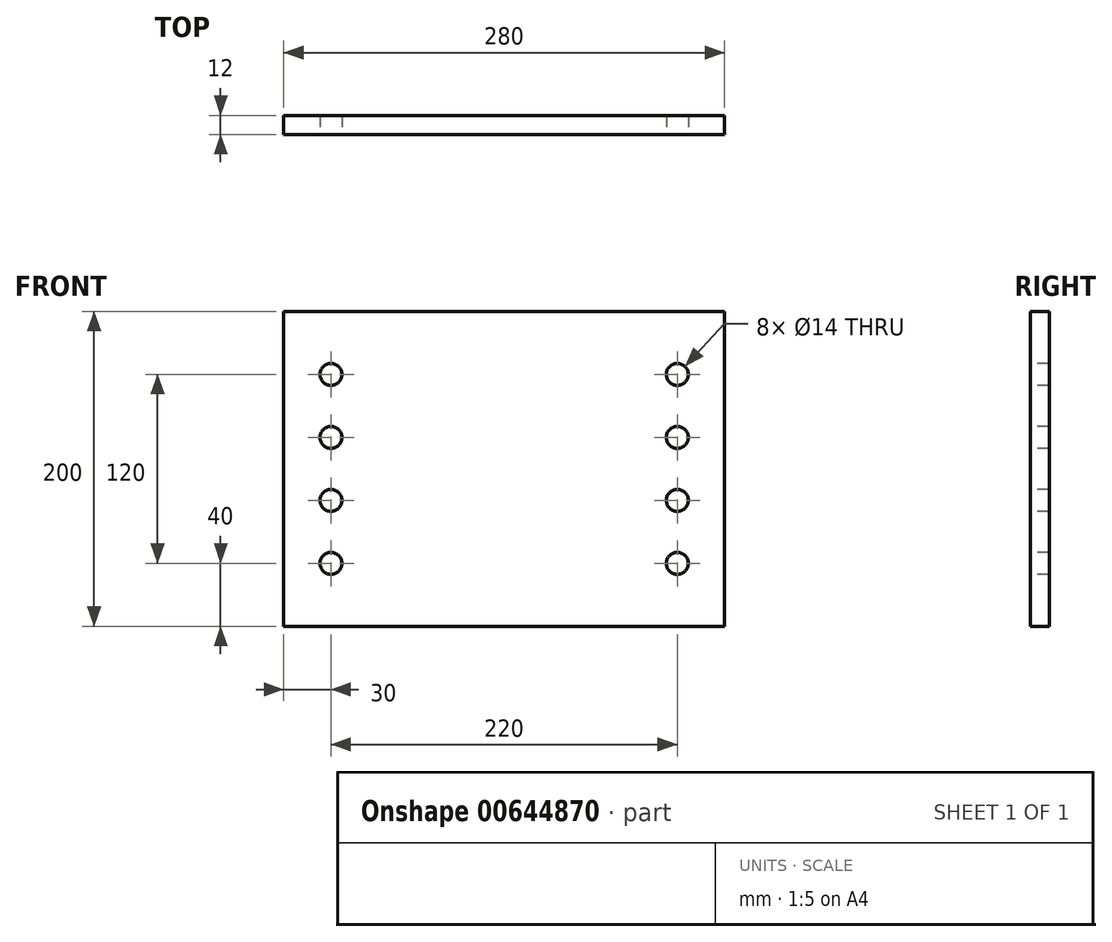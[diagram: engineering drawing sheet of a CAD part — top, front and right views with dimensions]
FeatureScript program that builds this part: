
annotation { "Feature Type Name" : "Feature", "Feature Type Description" : "" }
export const myFeature = defineFeature(function(context is Context, id is Id, definition is map)
    precondition{}
    {
        {
            var Q0;
            Q0=qCreatedBy(makeId("Front.planeOp"),FACE);
            var sketch = newSketch(context, id + "F0", { "sketchPlane" : qUnion([Q0])});
            skLineSegment(sketch, "E0.bottom", {"start": v(0, 0) * mm, "end": v(280, 0) * mm});
            skLineSegment(sketch, "E0.top", {"start": v(0, 200) * mm, "end": v(280, 200) * mm});
            skLineSegment(sketch, "E0.left", {"start": v(0, 0) * mm, "end": v(0, 200) * mm});
            skLineSegment(sketch, "E0.right", {"start": v(280, 0) * mm, "end": v(280, 200) * mm});
            skSolve(sketch);
        }
        {
            var Q0;
            Q0=makeQuery(id+"F0.imprint","IMPRINT",FACE,{"disambiguationData":[TD([[makeQuery(id+"F0.imprint","IMPRINT",EDGE,{"derivedFrom":sQuery(id+"F0.wireOp",EDGE,"E0.bottom")}),1.0]])]});
            extrude(context, id + "F1", {"entities" : qUnion([Q0]), "depth" : 12 * mm});
        }
        {
            var Q0;
            Q0=makeQuery(id+"F1.opExtrude","CAP_FACE",FACE,{"disambiguationData":[OSD([sQuery(id+"F0.wireOp",EDGE,"E0.bottom"),sQuery(id+"F0.wireOp",EDGE,"E0.top"),sQuery(id+"F0.wireOp",EDGE,"E0.left"),sQuery(id+"F0.wireOp",EDGE,"E0.right")])],"isStart":false});
            var sketch = newSketch(context, id + "F2", { "sketchPlane" : qUnion([Q0])});
            skLineSegment(sketch, "E1", {"start": v(30, 200) * mm, "end": v(30, 0) * mm});
            skLineSegment(sketch, "E2", {"start": v(250, 200) * mm, "end": v(250, 0) * mm});
            skLineSegment(sketch, "E3", {"start": v(0, 160) * mm, "end": v(280, 160) * mm});
            skLineSegment(sketch, "E4", {"start": v(0, 120) * mm, "end": v(280, 120) * mm});
            skLineSegment(sketch, "E5", {"start": v(0, 80) * mm, "end": v(280, 80) * mm});
            skLineSegment(sketch, "E6", {"start": v(0, 40) * mm, "end": v(280, 40) * mm});
            skPoint(sketch, "E7", {"position": v(30, 160) * mm});
            skPoint(sketch, "E8", {"position": v(30, 120) * mm});
            skPoint(sketch, "E9", {"position": v(30, 80) * mm});
            skPoint(sketch, "E10", {"position": v(30, 40) * mm});
            skPoint(sketch, "E11", {"position": v(250, 40) * mm});
            skPoint(sketch, "E12", {"position": v(250, 80) * mm});
            skPoint(sketch, "E13", {"position": v(250, 120) * mm});
            skPoint(sketch, "E14", {"position": v(250, 160) * mm});
            skSolve(sketch);
        }
        {
            var Q0;
            Q0=sQuery(id+"F2.wireOp",VERTEX,"E7");
            var Q1;
            Q1=sQuery(id+"F2.wireOp",VERTEX,"E8");
            var Q2;
            Q2=sQuery(id+"F2.wireOp",VERTEX,"E9");
            var Q3;
            Q3=sQuery(id+"F2.wireOp",VERTEX,"E10");
            var Q4;
            Q4=sQuery(id+"F2.wireOp",VERTEX,"E11");
            var Q5;
            Q5=sQuery(id+"F2.wireOp",VERTEX,"E12");
            var Q6;
            Q6=sQuery(id+"F2.wireOp",VERTEX,"E13");
            var Q7;
            Q7=sQuery(id+"F2.wireOp",VERTEX,"E14");
            var Q8;
            Q8=makeQuery(id+"F1.opExtrude","SWEPT_BODY",BODY,{"disambiguationData":[OSD([sQuery(id+"F0.wireOp",EDGE,"E0.bottom"),sQuery(id+"F0.wireOp",EDGE,"E0.top"),sQuery(id+"F0.wireOp",EDGE,"E0.left"),sQuery(id+"F0.wireOp",EDGE,"E0.right")])]});
            hole(context, id + "F3", {"style" : HoleStyle.SIMPLE, "endStyle" : HoleEndStyle.THROUGH, "holeDiameter" : 14 * mm, "tappedDepth" : 12 * mm, "tapClearance" : 3, "locations" : qUnion([Q0, Q1, Q2, Q3, Q4, Q5, Q6, Q7]), "scope" : qUnion([Q8])});
        }
    });
